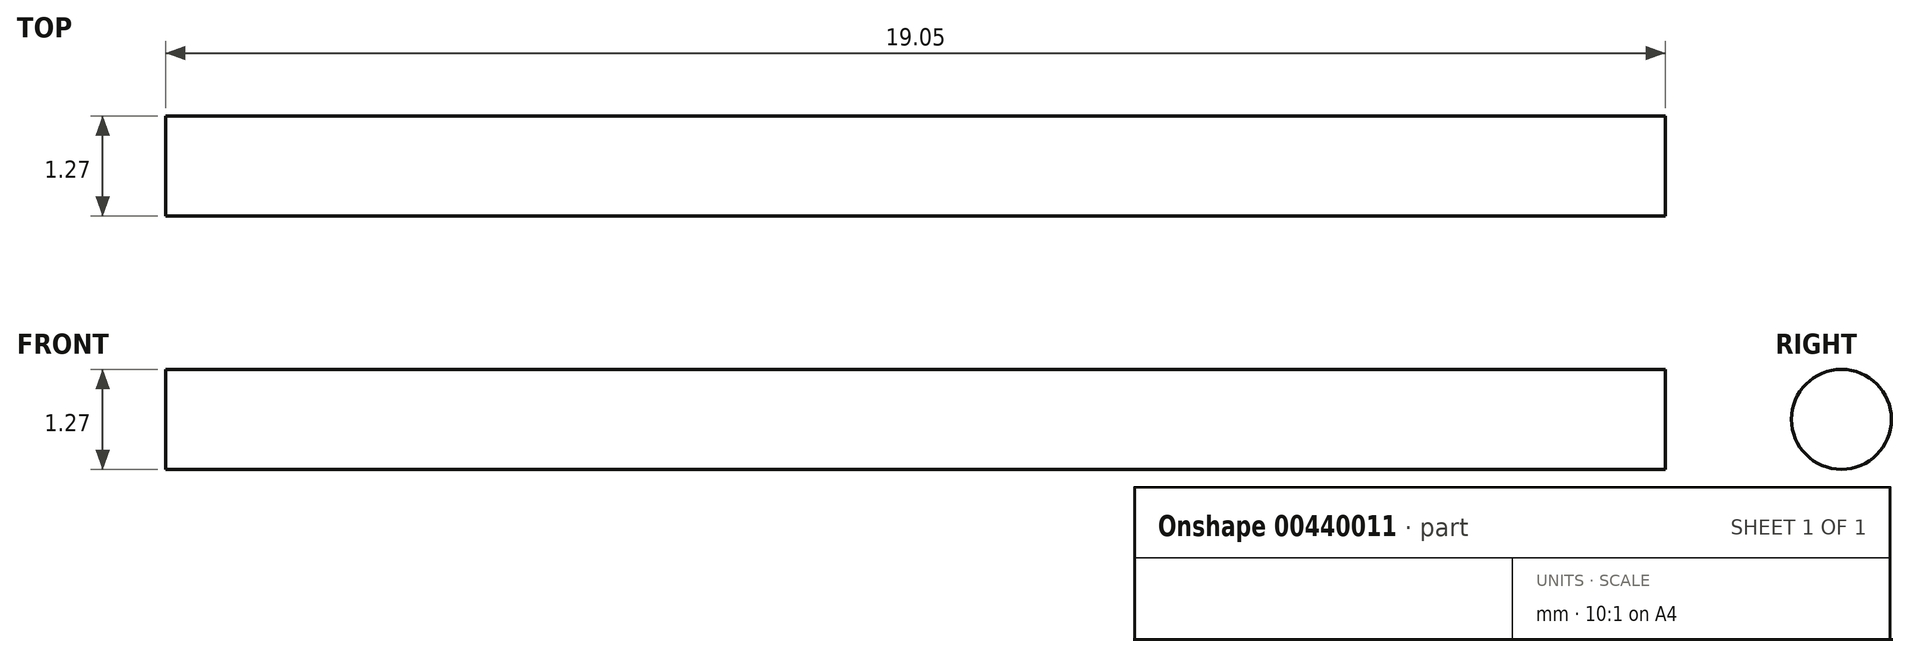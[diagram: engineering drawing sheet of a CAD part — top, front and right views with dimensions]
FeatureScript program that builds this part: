
annotation { "Feature Type Name" : "Feature", "Feature Type Description" : "" }
export const myFeature = defineFeature(function(context is Context, id is Id, definition is map)
    precondition{}
    {
        {
            var Q0;
            Q0=qCreatedBy(makeId("Right.planeOp"),FACE);
            var sketch = newSketch(context, id + "F0", { "sketchPlane" : qUnion([Q0])});
            skCircle(sketch, "E0", {"center": v(-26.73, 20.1) * mm, "radius": 0.64 * mm});
            skSolve(sketch);
        }
        {
            var Q0;
            Q0=makeQuery(id+"F0.imprint","IMPRINT",FACE,{"disambiguationData":[TD([[makeQuery(id+"F0.imprint","IMPRINT",EDGE,{"derivedFrom":sQuery(id+"F0.wireOp",EDGE,"E0")}),1.0]])]});
            extrude(context, id + "F1", {"entities" : qUnion([Q0]), "depth" : 19.05 * mm});
        }
    });
